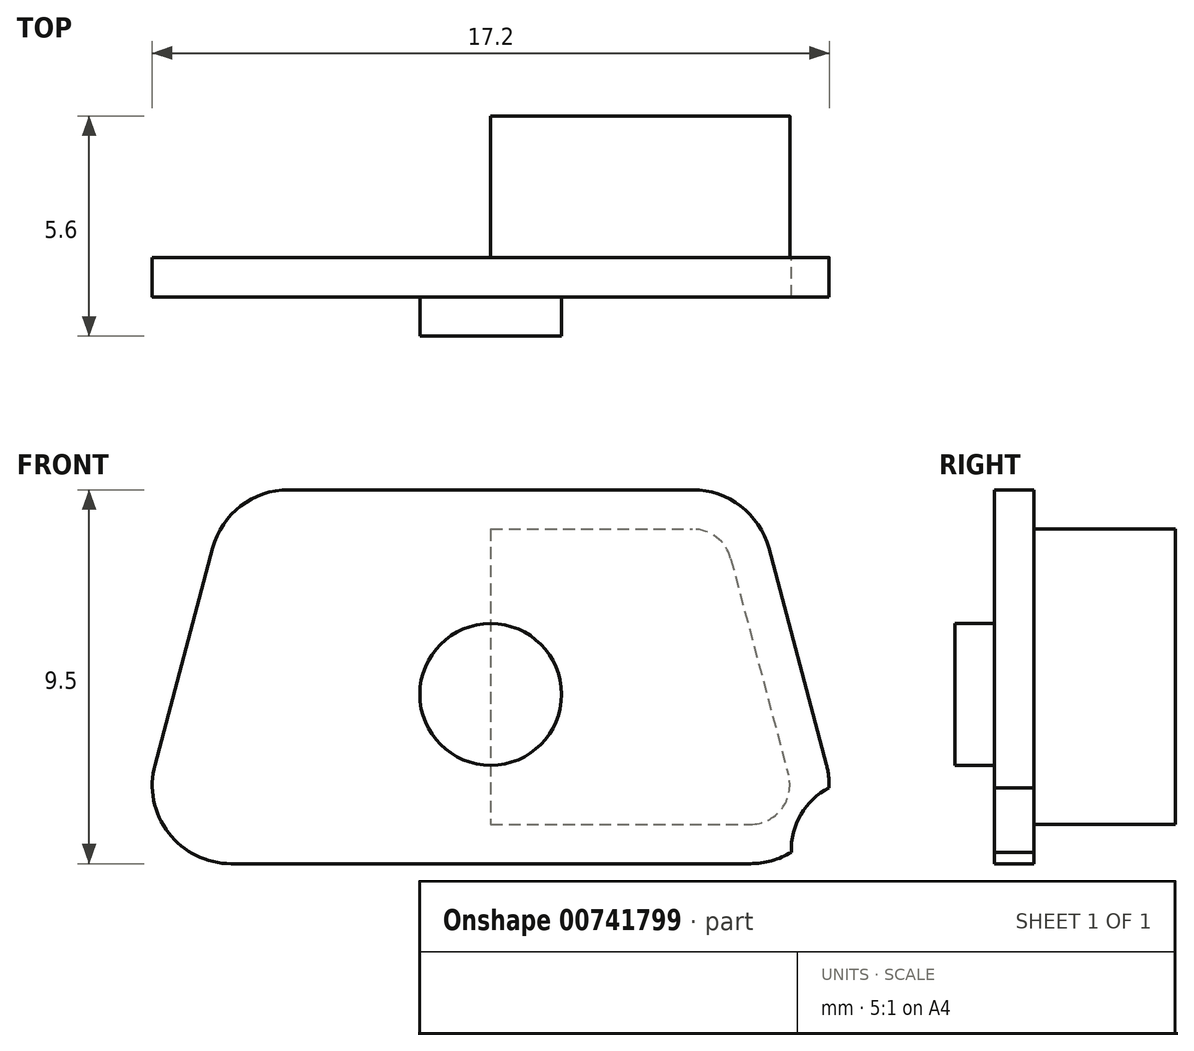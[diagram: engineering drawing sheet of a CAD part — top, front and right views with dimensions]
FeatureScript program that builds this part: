
annotation { "Feature Type Name" : "Feature", "Feature Type Description" : "" }
export const myFeature = defineFeature(function(context is Context, id is Id, definition is map)
    precondition{}
    {
        {
            var Q0;
            Q0=qCreatedBy(makeId("Front.planeOp"),FACE);
            var sketch = newSketch(context, id + "F0", { "sketchPlane" : qUnion([Q0])});
            skLineSegment(sketch, "E0", {"start": v(0, 0) * mm, "end": v(6.6, 0) * mm});
            skLineSegment(sketch, "E1", {"start": v(0, 7.5) * mm, "end": v(5.13, 7.5) * mm});
            skLineSegment(sketch, "E2", {"start": v(6.1, 6.76) * mm, "end": v(7.56, 1.26) * mm});
            skPoint(sketch, "E3.visualSharp", {"position": v(5.9, 7.5) * mm});
            skArc(sketch, "E3.filletArc", {"start": v(6.1, 6.76) * mm, "mid": v(5.74, 7.3) * mm, "end": v(5.13, 7.5) * mm});
            skPoint(sketch, "E4.visualSharp", {"position": v(7.9, 0) * mm});
            skArc(sketch, "E4.filletArc", {"start": v(6.6, 0) * mm, "mid": v(7.4, 0.4) * mm, "end": v(7.56, 1.26) * mm});
            skLineSegment(sketch, "E5", {"start": v(0, 7.5) * mm, "end": v(0, 0) * mm});
            skSolve(sketch);
        }
        {
            var Q0;
            Q0=makeQuery(id+"F0.imprint","IMPRINT",FACE,{"disambiguationData":[TD([[makeQuery(id+"F0.imprint","IMPRINT",EDGE,{"derivedFrom":sQuery(id+"F0.wireOp",EDGE,"E0")}),1.0]])]});
            var Q1;
            Q1=makeQuery(id+"FoUKuCBFI7obaB1_0.1.F0.imprint","IMPRINT",FACE,{"disambiguationData":[TD([[makeQuery(id+"FoUKuCBFI7obaB1_0.1.F0.imprint","IMPRINT",EDGE,{"derivedFrom":sQuery(id+"FoUKuCBFI7obaB1_0.1.F0.wireOp",EDGE,"E0")}),1.0]])]});
            extrude(context, id + "F1", {"entities" : qUnion([Q0, Q1]), "depth" : 3.6 * mm, "offsetDistance" : 25 * mm});
        }
        {
            var Q0;
            Q0=makeQuery(id+"F1.opExtrude","CAP_FACE",FACE,{"disambiguationData":[OSD([sQuery(id+"F0.wireOp",EDGE,"E0"),sQuery(id+"F0.wireOp",EDGE,"E1"),sQuery(id+"F0.wireOp",EDGE,"E2"),sQuery(id+"F0.wireOp",EDGE,"E3.filletArc"),sQuery(id+"F0.wireOp",EDGE,"E4.filletArc"),sQuery(id+"F0.wireOp",EDGE,"E5")])],"isStart":false});
            var sketch = newSketch(context, id + "F2", { "sketchPlane" : qUnion([Q0])});
            skArc(sketch, "E6.0", {"start": v(6.6, -1) * mm, "mid": v(8.18, -0.22) * mm, "end": v(8.53, 1.52) * mm});
            skArc(sketch, "E6.1", {"start": v(7.06, 7.02) * mm, "mid": v(6.35, 8.09) * mm, "end": v(5.13, 8.5) * mm});
            skLineSegment(sketch, "E6.2", {"start": v(5.13, 8.5) * mm, "end": v(-1, 8.5) * mm});
            skLineSegment(sketch, "E6.3", {"start": v(8.53, 1.52) * mm, "end": v(7.06, 7.02) * mm});
            skLineSegment(sketch, "E6.4", {"start": v(-1, 8.5) * mm, "end": v(-1, -1) * mm});
            skLineSegment(sketch, "E6.5", {"start": v(-1, -1) * mm, "end": v(6.6, -1) * mm});
            skArc(sketch, "E7.0", {"start": v(-5.13, 8.5) * mm, "mid": v(-6.35, 8.09) * mm, "end": v(-7.06, 7.02) * mm});
            skArc(sketch, "E7.1", {"start": v(-8.53, 1.52) * mm, "mid": v(-8.18, -0.22) * mm, "end": v(-6.6, -1) * mm});
            skLineSegment(sketch, "E7.2", {"start": v(-6.6, -1) * mm, "end": v(1, -1) * mm});
            skLineSegment(sketch, "E7.3", {"start": v(-7.06, 7.02) * mm, "end": v(-8.53, 1.52) * mm});
            skLineSegment(sketch, "E7.4", {"start": v(1, -1) * mm, "end": v(1, 8.5) * mm});
            skLineSegment(sketch, "E7.5", {"start": v(1, 8.5) * mm, "end": v(-5.13, 8.5) * mm});
            skSolve(sketch);
        }
        {
            var Q0;
            Q0 = qSketchRegion(id + "F2", true);
            extrude(context, id + "F3", {"entities" : qUnion([Q0]), "depth" : 1 * mm, "offsetDistance" : 25 * mm});
        }
        {
            var Q0;
            Q0=makeQuery(id+"F3.opExtrude","CAP_FACE",FACE,{"disambiguationData":[OSD([sQuery(id+"F2.wireOp",EDGE,"E6.0"),sQuery(id+"F2.wireOp",EDGE,"E6.1"),sQuery(id+"F2.wireOp",EDGE,"E6.2"),sQuery(id+"F2.wireOp",EDGE,"E6.3"),sQuery(id+"F2.wireOp",EDGE,"E6.5"),sQuery(id+"F2.wireOp",EDGE,"E7.0"),sQuery(id+"F2.wireOp",EDGE,"E7.1"),sQuery(id+"F2.wireOp",EDGE,"E7.2"),sQuery(id+"F2.wireOp",EDGE,"E7.3"),sQuery(id+"F2.wireOp",EDGE,"E7.5")])],"isStart":true});
            var sketch = newSketch(context, id + "F4", { "sketchPlane" : qUnion([Q0])});
            skCircle(sketch, "E8", {"center": v(-9.38, -0.63) * mm, "radius": 1.74 * mm});
            skSolve(sketch);
        }
        {
            var Q0;
            Q0 = qSketchRegion(id + "F4", true);
            extrude(context, id + "F5", {"entities" : qUnion([Q0]), "operationType" : NewBodyOperationType.REMOVE, "oppositeDirection" : true, "depth" : 25 * mm, "offsetDistance" : 25 * mm});
        }
        {
            var Q0;
            Q0=makeQuery(id+"F3.opExtrude","CAP_FACE",FACE,{"disambiguationData":[OSD([sQuery(id+"F2.wireOp",EDGE,"E6.0"),sQuery(id+"F2.wireOp",EDGE,"E6.1"),sQuery(id+"F2.wireOp",EDGE,"E6.2"),sQuery(id+"F2.wireOp",EDGE,"E6.3"),sQuery(id+"F2.wireOp",EDGE,"E6.5"),sQuery(id+"F2.wireOp",EDGE,"E7.0"),sQuery(id+"F2.wireOp",EDGE,"E7.1"),sQuery(id+"F2.wireOp",EDGE,"E7.2"),sQuery(id+"F2.wireOp",EDGE,"E7.3"),sQuery(id+"F2.wireOp",EDGE,"E7.5")])],"isStart":false});
            var sketch = newSketch(context, id + "F6", { "sketchPlane" : qUnion([Q0])});
            skCircle(sketch, "E9", {"center": v(0, 3.3) * mm, "radius": 1.8 * mm});
            skPoint(sketch, "E9.centerSnap0", {"position": v(0, 8.5) * mm});
            skSolve(sketch);
        }
        {
            var Q0;
            Q0 = qSketchRegion(id + "F6", true);
            extrude(context, id + "F7", {"entities" : qUnion([Q0]), "operationType" : NewBodyOperationType.ADD, "depth" : 1 * mm, "offsetDistance" : 25 * mm});
        }
    });
